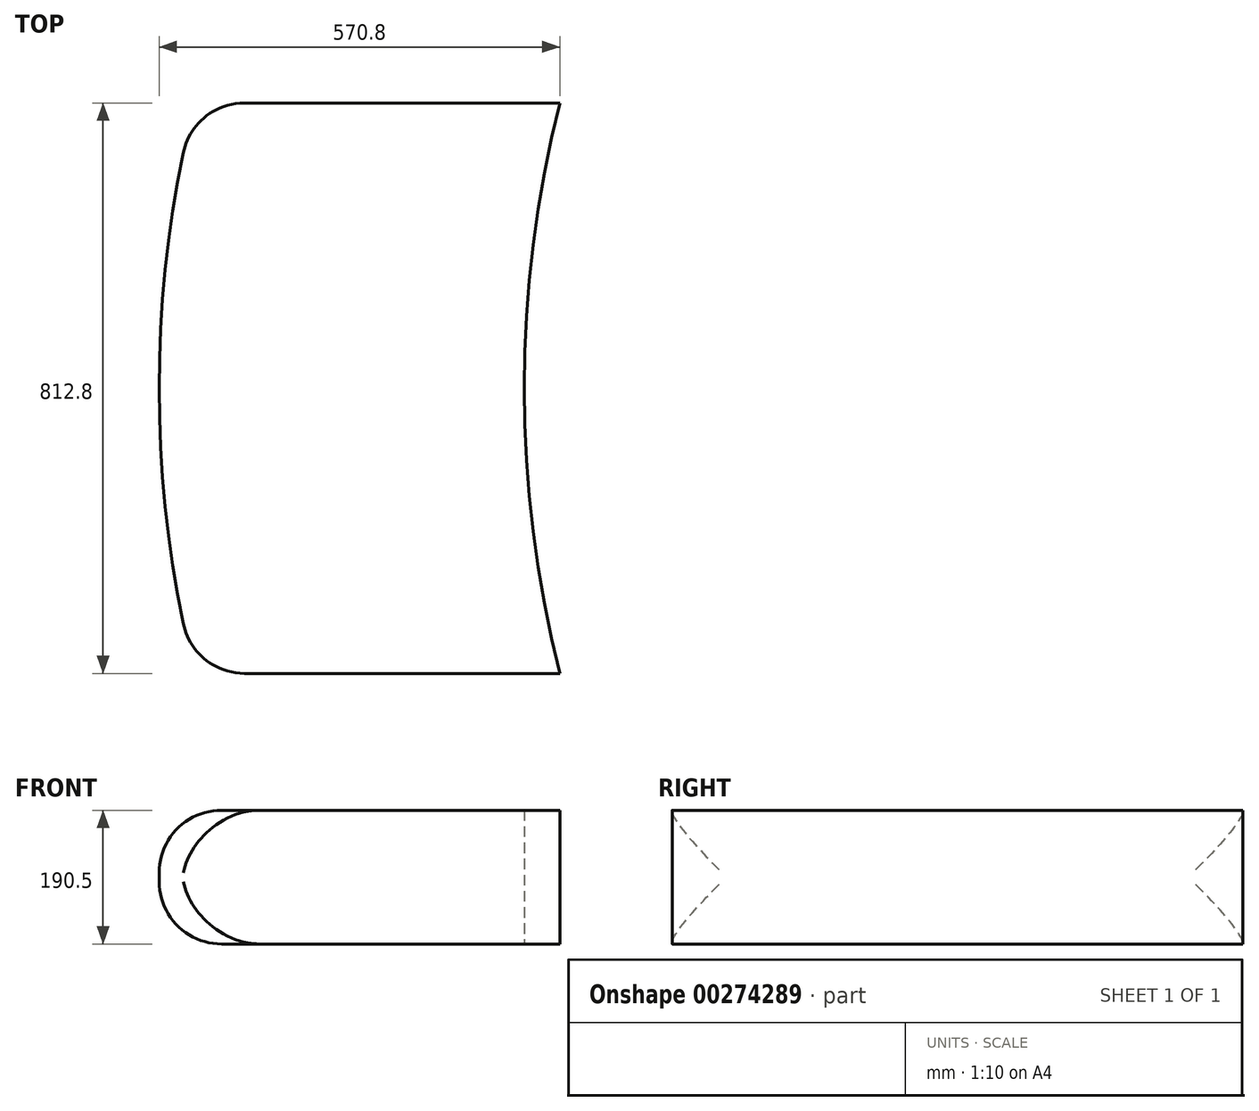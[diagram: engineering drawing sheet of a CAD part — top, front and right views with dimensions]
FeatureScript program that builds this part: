
annotation { "Feature Type Name" : "Feature", "Feature Type Description" : "" }
export const myFeature = defineFeature(function(context is Context, id is Id, definition is map)
    precondition{}
    {
        {
            var Q0;
            Q0=qCreatedBy(makeId("Top.planeOp"),FACE);
            var sketch = newSketch(context, id + "F0", { "sketchPlane" : qUnion([Q0])});
            skLineSegment(sketch, "E0", {"start": v(0, 0) * mm, "end": v(0, 406.4) * mm});
            skLineSegment(sketch, "E1", {"start": v(0, 0) * mm, "end": v(0, -406.4) * mm});
            skLineSegment(sketch, "E2", {"start": v(0, -406.4) * mm, "end": v(520, -406.4) * mm});
            skLineSegment(sketch, "E3", {"start": v(0, 406.4) * mm, "end": v(519.99, 406.4) * mm});
            skArc(sketch, "E4", {"start": v(519.99, 406.4) * mm, "mid": v(469.2, 0) * mm, "end": v(520, -406.4) * mm});
            skArc(sketch, "E5", {"start": v(0, 406.4) * mm, "mid": v(-50.8, 0) * mm, "end": v(0, -406.4) * mm});
            skSolve(sketch);
        }
        {
            var Q0;
            Q0 = qSketchRegion(id + "F0", true);
            extrude(context, id + "F1", {"entities" : qUnion([Q0]), "depth" : 190.5 * mm});
        }
        {
            var Q0;
            Q0=makeQuery(id+"F1.opExtrude","SWEPT_FACE",FACE,{"disambiguationData":[OSD([sQuery(id+"F0.wireOp",EDGE,"E5")])]});
            fillet(context, id + "F2", {"entities" : qUnion([Q0]), "radius" : 88.9 * mm, "tangentPropagation" : true, "allowEdgeOverflow" : false});
        }
    });
